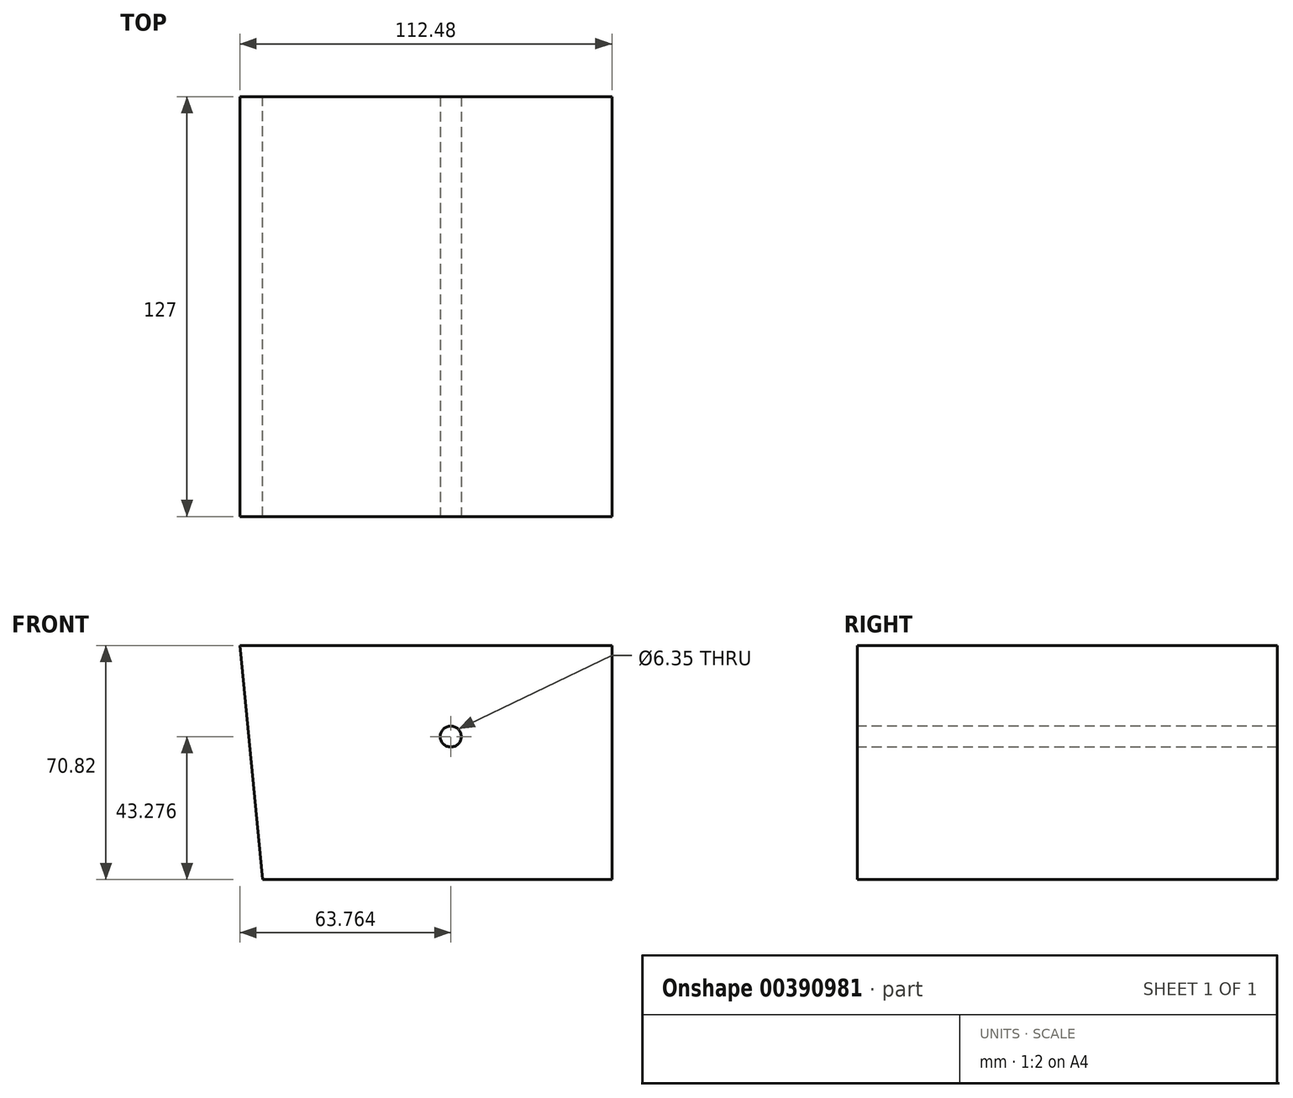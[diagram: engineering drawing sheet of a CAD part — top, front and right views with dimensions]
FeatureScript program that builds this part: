
annotation { "Feature Type Name" : "Feature", "Feature Type Description" : "" }
export const myFeature = defineFeature(function(context is Context, id is Id, definition is map)
    precondition{}
    {
        {
            var Q0;
            Q0=qCreatedBy(makeId("Front.planeOp"),FACE);
            var sketch = newSketch(context, id + "F0", { "sketchPlane" : qUnion([Q0])});
            skLineSegment(sketch, "E0", {"start": v(-57.1, 44.23) * mm, "end": v(55.38, 44.23) * mm});
            skLineSegment(sketch, "E1", {"start": v(55.38, 44.23) * mm, "end": v(55.38, -26.59) * mm});
            skLineSegment(sketch, "E2", {"start": v(55.38, -26.59) * mm, "end": v(-50.24, -26.59) * mm});
            skLineSegment(sketch, "E3", {"start": v(-50.24, -26.59) * mm, "end": v(-57.1, 44.23) * mm});
            skSolve(sketch);
        }
        {
            var Q0;
            Q0=makeQuery(id+"F0.imprint","IMPRINT",FACE,{"disambiguationData":[TD([[makeQuery(id+"F0.imprint","IMPRINT",EDGE,{"derivedFrom":sQuery(id+"F0.wireOp",EDGE,"E0")}),-1.0]])]});
            extrude(context, id + "F1", {"entities" : qUnion([Q0]), "depth" : 127 * mm});
        }
        {
            var Q0;
            Q0=makeQuery(id+"F1.opExtrude","CAP_FACE",FACE,{"disambiguationData":[OSD([sQuery(id+"F0.wireOp",EDGE,"E0"),sQuery(id+"F0.wireOp",EDGE,"E1"),sQuery(id+"F0.wireOp",EDGE,"E2"),sQuery(id+"F0.wireOp",EDGE,"E3")])],"isStart":false});
            var sketch = newSketch(context, id + "F2", { "sketchPlane" : qUnion([Q0])});
            skCircle(sketch, "E4", {"center": v(6.66, 16.69) * mm, "radius": 11.5 * mm});
            skSolve(sketch);
        }
        {
            var Q0;
            Q0=sQuery(id+"F2.wireOp",VERTEX,"E4.center");
            var Q1;
            Q1=makeQuery(id+"F1.opExtrude","SWEPT_BODY",BODY,{"disambiguationData":[OSD([sQuery(id+"F0.wireOp",EDGE,"E0"),sQuery(id+"F0.wireOp",EDGE,"E1"),sQuery(id+"F0.wireOp",EDGE,"E2"),sQuery(id+"F0.wireOp",EDGE,"E3")])]});
            hole(context, id + "F3", {"style" : HoleStyle.SIMPLE, "endStyle" : HoleEndStyle.THROUGH, "holeDiameter" : 6.35 * mm, "isTappedThrough" : true, "tappedDepth" : 12.7 * mm, "tapClearance" : 3, "locations" : qUnion([Q0]), "scope" : qUnion([Q1])});
        }
    });
